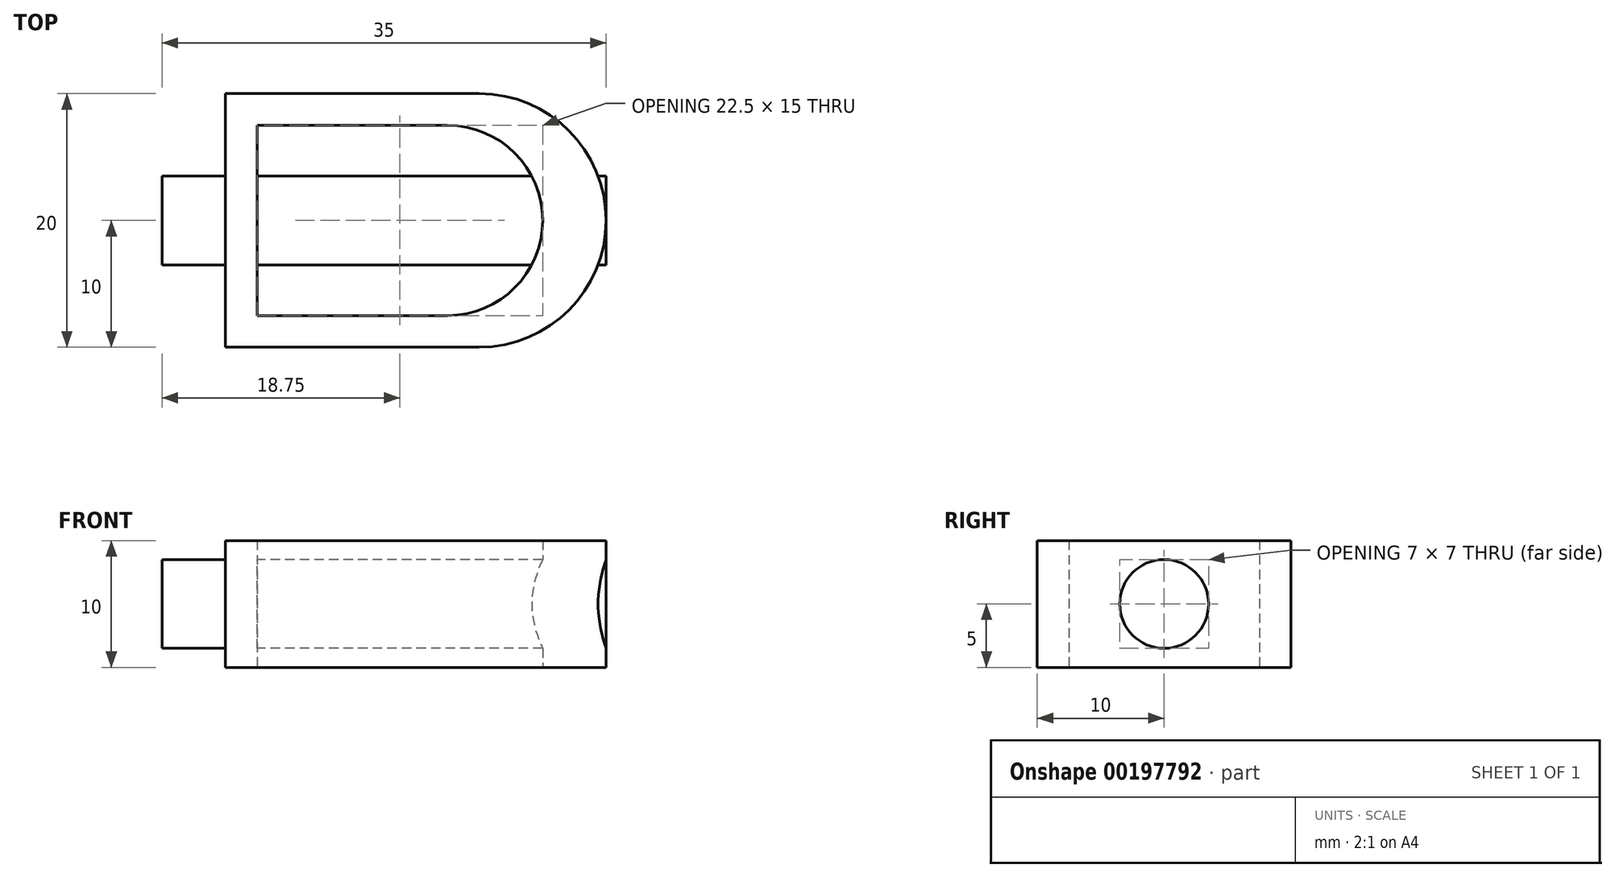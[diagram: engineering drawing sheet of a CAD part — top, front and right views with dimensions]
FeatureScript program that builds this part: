
annotation { "Feature Type Name" : "Feature", "Feature Type Description" : "" }
export const myFeature = defineFeature(function(context is Context, id is Id, definition is map)
    precondition{}
    {
        {
            var Q0;
            Q0=qCreatedBy(makeId("Top.planeOp"),FACE);
            var sketch = newSketch(context, id + "F0", { "sketchPlane" : qUnion([Q0])});
            skLineSegment(sketch, "E0.bottom", {"start": v(10, 10) * mm, "end": v(-10, 10) * mm});
            skLineSegment(sketch, "E0.top", {"start": v(10, -10) * mm, "end": v(-10, -10) * mm});
            skLineSegment(sketch, "E0.left", {"start": v(10, 10) * mm, "end": v(10, -10) * mm});
            skLineSegment(sketch, "E0.right", {"start": v(-10, 10) * mm, "end": v(-10, -10) * mm});
            skPoint(sketch, "E0.middle", {"position": v(0, 0) * mm});
            skLineSegment(sketch, "E1.bottom", {"start": v(7.5, 7.5) * mm, "end": v(-7.5, 7.5) * mm});
            skLineSegment(sketch, "E1.top", {"start": v(7.5, -7.5) * mm, "end": v(-7.5, -7.5) * mm});
            skLineSegment(sketch, "E1.left", {"start": v(7.5, 7.5) * mm, "end": v(7.5, -7.5) * mm});
            skLineSegment(sketch, "E1.right", {"start": v(-7.5, 7.5) * mm, "end": v(-7.5, -7.5) * mm});
            skCircle(sketch, "E2", {"center": v(10, 0) * mm, "radius": 10 * mm});
            skCircle(sketch, "E3", {"center": v(7.5, 0) * mm, "radius": 7.5 * mm});
            skSolve(sketch);
        }
        {
            var Q0;
            Q0 = qSketchRegion(id + "F0", true);
            extrude(context, id + "F1", {"entities" : qUnion([Q0]), "depth" : 10 * mm});
        }
        {
            var Q0;
            Q0=makeQuery(id+"F1.opExtrude","SWEPT_BODY",BODY,{"disambiguationData":[OSD([sQuery(id+"F0.wireOp",EDGE,"E0.bottom"),sQuery(id+"F0.wireOp",EDGE,"E0.top"),sQuery(id+"F0.wireOp",EDGE,"E0.right"),sQuery(id+"F0.wireOp",EDGE,"E1.bottom"),sQuery(id+"F0.wireOp",EDGE,"E1.top"),sQuery(id+"F0.wireOp",EDGE,"E1.right"),sQuery(id+"F0.wireOp",EDGE,"E2"),sQuery(id+"F0.wireOp",EDGE,"E3")])]});
            transform(context, id + "F2", {"entities" : qUnion([Q0]), "transformType" : TransformType.TRANSLATION_3D, "dx" : 0 * mm, "dy" : 0 * mm, "dz" : -5 * mm, "makeCopy" : false});
        }
        {
            var Q0;
            Q0=makeQuery(id+"F1.opExtrude","SWEPT_FACE",FACE,{"disambiguationData":[OSD([sQuery(id+"F0.wireOp",EDGE,"E0.right")])]});
            var sketch = newSketch(context, id + "F3", { "sketchPlane" : qUnion([Q0])});
            skCircle(sketch, "E4", {"center": v(0, 0) * mm, "radius": 3.5 * mm});
            skSolve(sketch);
        }
        {
            var Q0;
            Q0 = qSketchRegion(id + "F3", true);
            extrude(context, id + "F4", {"entities" : qUnion([Q0]), "operationType" : NewBodyOperationType.ADD, "oppositeDirection" : true, "depth" : 30 * mm, "hasSecondDirection" : true, "secondDirectionOppositeDirection" : false, "secondDirectionDepth" : 5 * mm});
        }
    });
